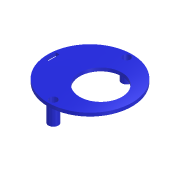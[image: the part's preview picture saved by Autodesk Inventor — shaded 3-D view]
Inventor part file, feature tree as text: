
AUTODESK INVENTOR PART (.ipt)
format: ipt  version: 2018 (Build 220112000, 112)  size: 145,920 bytes
history: native  units: mm
features: extrude x6, sketch x6, mirror x1
ambient origin geometry x8: Origin, YZ Plane, XZ Plane, XY Plane, X Axis, Y Axis, Z Axis, Center Point
bodies: Solid1 (feature_tree)
feature tree (13):
  extrude  "Extrusion1"  Depth=3.0mm TaperAngle=0.0deg
  extrude  "Extrusion2"  Depth=3.0mm TaperAngle=0.0deg
  mirror  "Mirror1"
  extrude  "Extrusion3"  Depth=9.0mm
  extrude  "Extrusion4"  Depth=15.0mm
  extrude  "Extrusion5"  Depth=18.5mm TaperAngle=0.0deg
  extrude  "Extrusion6"  Depth=10.0mm
  sketch  "Sketch1"  dims[d0=75.7mm d1=3.0mm d2=0.0mm]
  sketch  "Sketch2"  dims[d3=33.02mm d4=6.8mm d5=3.0mm d6=0.0mm]
  sketch  "Sketch3"  dims[d7=9.0mm d8=9.0mm]
  sketch  "Sketch4"  dims[d9=15.0mm d10=0.0mm d11=9.736mm]
  sketch  "Sketch5"  dims[d12=38.0mm d13=18.5mm d14=0.0mm]
  sketch  "Sketch6"  dims[d15=8.554mm d16=42.0mm d17=18.5mm d18=0.0mm d19=10.0mm d20=5.0mm d21=3.5mm d22=36.0mm d23=10.0mm d24=0.0mm]
